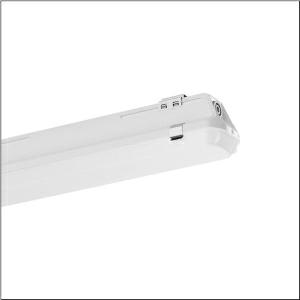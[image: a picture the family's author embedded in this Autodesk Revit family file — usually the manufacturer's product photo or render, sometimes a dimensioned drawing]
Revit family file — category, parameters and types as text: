
# Revit family: monsun_r__21_51fb10dl440j_1afc
name_source: partatom
category: Lighting Fixtures
units: mm (PartAtom-declared; Revit-internal decimal feet)

## family parameters
Cut with Voids When Loaded = No
Host = Face
Light Source = No
Part Type = Normal
Room Calculation Point = No
Round Connector Dimension = Use Diameter
Shared = No

## types (1)
- --- (1 x LED, 4330 lm, 26.8 W, 4000K)
    Apparent Load = 27 VA
    CIE Flux Codes = 46 76 93 94 100
    Color Rendering = 80
    Color Temperature = 4000K
    Default Elevation = 1800 mm
    Description = Monsun® 21, damp-proof luminaire, chain hanger, primary optical cover: enclosure, of PMMA, light emission: direct distribution, primary light characteristic: symmetric, installation type: suspended mounting, surface-mounted, horizontal mounting, vertical mounting, LED, rated luminous flux: 4.330lm, luminous efficacy: 160lm/W, light colour: 840, colour temperature: 4000K, control gear: ECG DALI, with terminal, 5-pole, max. 2.5mm², mains connection: 220..240V, AC, 50/60Hz, rated input power: 27W, housing, of glass-fibre reinforced plastic, uncoated, bright grey, incl. chain hanger, length: 1.299mm, width: 90mm, height: 88mm, clip for enclosure, of stainless steel (V2A), ceiling mounting element, of stainless steel (V2A), chain hanger, of stainless steel (V2A), protection rating (complete): IP66, insulation class (complete): insulation class I (protective earthing), certification: CE, ENEC, VDE, UKCA, protection symbol: D, impact resistance: IK04, permissible operating ambient temperature: -25..+35°C, standard: EN 50419, EN 60598-2-1, corresponds to IFS (International Featured Standards) requirements for safety and quality in the food industry, for indoor or canopied outdoor use, no direct snow, no direct sun, no direct rain, contact your sales advisor before using the luminaires in applications with unclear chemical exposure, large temperature fluctuations or condensation-forming humidity, LABS conformity tested according to VDMA 24364:2018-05, packaging unit: 1 piece
    Height = 88 mm
    Lamp = 1 x LED
    Lamp Light Flux = 4330 lm
    Lamp Power = 26.8 W
    Lamp count = 1
    Length = 1299 mm
    Luminous efficacy = 162 lm/W
    Manufacturer = Siteco
    ModVariant = No
    Model = 51FB10DL440J
    Mounting Place = Ceiling
    Mounting Type = Surface mounted
    Number of Poles = 1
    OnlyDefault = Yes
    Power Factor = 1
    Product Name = Monsun® 21
    Product group = damp-proof luminaire
    ProductGroupID = 300
    Protection Class = Protection class I
    Protection Degree = IP 66
    RLX_Detail_Level = 1
    RLX_Emergency_Light_Flux = 0 lm
    RLX_Emergency_Type = 0
    RLX_Emergency_Type_DB = No
    RlxData = <blob elided: 93321 chars, md5=73d0b646>
    Socket = socket
    Standby Power = 0 W
    System Light Flux = 4330 lm
    System Power = 27 W
    Type Comments = factory setting: luminous flux: 100 % | dim-lin: 254 | 179 mA
    Type Image = l_1006717.jpg
    URL = http://relux.com
    VarID = @adj_077991
    Voltage = 0 V
    Weight = 0.00 kg
    Width = 90 mm

## geometry (parser evidence)
native form markers: Blend x4, Sweep x12
no freeform markers — native parametric forms only
